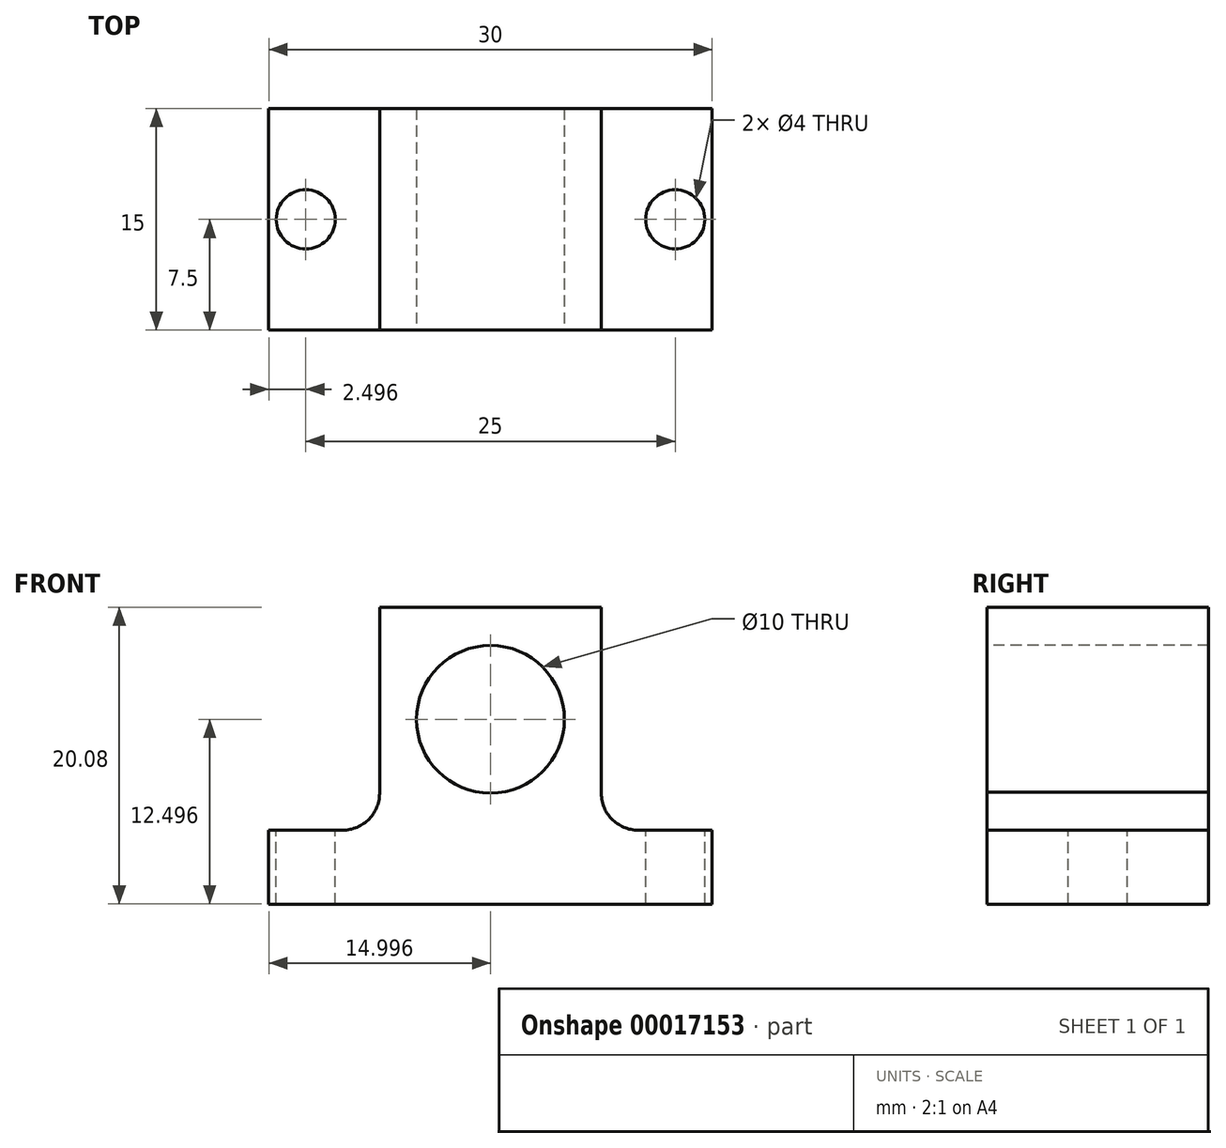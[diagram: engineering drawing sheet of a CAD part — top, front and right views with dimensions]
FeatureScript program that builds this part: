
annotation { "Feature Type Name" : "Feature", "Feature Type Description" : "" }
export const myFeature = defineFeature(function(context is Context, id is Id, definition is map)
    precondition{}
    {
        {
            var Q0;
            Q0=qCreatedBy(makeId("Front.planeOp"),FACE);
            var sketch = newSketch(context, id + "F0", { "sketchPlane" : qUnion([Q0])});
            skLineSegment(sketch, "E0", {"start": v(-20.16, -31.2) * mm, "end": v(9.84, -31.2) * mm});
            skLineSegment(sketch, "E1", {"start": v(9.84, -31.2) * mm, "end": v(9.84, -26.2) * mm});
            skLineSegment(sketch, "E2", {"start": v(9.84, -26.2) * mm, "end": v(4.84, -26.2) * mm});
            skLineSegment(sketch, "E3", {"start": v(-20.16, -31.2) * mm, "end": v(-20.16, -26.2) * mm});
            skLineSegment(sketch, "E4", {"start": v(-20.16, -26.2) * mm, "end": v(-15.16, -26.2) * mm});
            skArc(sketch, "E5", {"start": v(4.84, -26.2) * mm, "mid": v(3.04, -25.44) * mm, "end": v(2.33, -23.62) * mm});
            skArc(sketch, "E6", {"start": v(-15.16, -26.2) * mm, "mid": v(-13.37, -25.44) * mm, "end": v(-12.67, -23.62) * mm});
            skLineSegment(sketch, "E7", {"start": v(-12.67, -23.62) * mm, "end": v(-12.67, -11.12) * mm});
            skLineSegment(sketch, "E8", {"start": v(-12.67, -11.12) * mm, "end": v(2.33, -11.12) * mm});
            skLineSegment(sketch, "E9", {"start": v(2.33, -11.12) * mm, "end": v(2.33, -23.62) * mm});
            skSolve(sketch);
        }
        {
            var Q0;
            Q0=makeQuery(id+"F0.imprint","IMPRINT",FACE,{"disambiguationData":[TD([[makeQuery(id+"F0.imprint","IMPRINT",EDGE,{"derivedFrom":sQuery(id+"F0.wireOp",EDGE,"E0")}),1.0]])]});
            extrude(context, id + "F1", {"entities" : qUnion([Q0]), "depth" : 15 * mm});
        }
        {
            var Q0;
            Q0=makeQuery(id+"F1.opExtrude","SWEPT_FACE",FACE,{"disambiguationData":[OSD([sQuery(id+"F0.wireOp",EDGE,"E4")])]});
            var sketch = newSketch(context, id + "F2", { "sketchPlane" : qUnion([Q0])});
            skCircle(sketch, "E10", {"center": v(-17.66, -7.5) * mm, "radius": 2 * mm});
            skSolve(sketch);
        }
        {
            var Q0;
            Q0=makeQuery(id+"F2.imprint","IMPRINT",FACE,{"disambiguationData":[TD([[makeQuery(id+"F2.imprint","IMPRINT",EDGE,{"derivedFrom":sQuery(id+"F2.wireOp",EDGE,"E10")}),1.0]])]});
            extrude(context, id + "F3", {"entities" : qUnion([Q0]), "operationType" : NewBodyOperationType.REMOVE, "endBound" : BoundingType.THROUGH_ALL, "oppositeDirection" : true, "depth" : 25 * mm});
        }
        {
            var Q0;
            Q0=makeQuery(id+"F1.opExtrude","SWEPT_FACE",FACE,{"disambiguationData":[OSD([sQuery(id+"F0.wireOp",EDGE,"E2")])]});
            var sketch = newSketch(context, id + "F4", { "sketchPlane" : qUnion([Q0])});
            skCircle(sketch, "E11", {"center": v(7.34, -7.5) * mm, "radius": 2 * mm});
            skSolve(sketch);
        }
        {
            var Q0;
            Q0 = qSketchRegion(id + "F4", true);
            extrude(context, id + "F5", {"entities" : qUnion([Q0]), "operationType" : NewBodyOperationType.REMOVE, "endBound" : BoundingType.THROUGH_ALL, "oppositeDirection" : true, "depth" : 25 * mm});
        }
        {
            var Q0;
            Q0=makeQuery(id+"F1.opExtrude","CAP_FACE",FACE,{"disambiguationData":[OSD([sQuery(id+"F0.wireOp",EDGE,"E0"),sQuery(id+"F0.wireOp",EDGE,"E1"),sQuery(id+"F0.wireOp",EDGE,"E2"),sQuery(id+"F0.wireOp",EDGE,"E3"),sQuery(id+"F0.wireOp",EDGE,"E4"),sQuery(id+"F0.wireOp",EDGE,"E5"),sQuery(id+"F0.wireOp",EDGE,"E6"),sQuery(id+"F0.wireOp",EDGE,"E7"),sQuery(id+"F0.wireOp",EDGE,"E8"),sQuery(id+"F0.wireOp",EDGE,"E9")])],"isStart":false});
            var sketch = newSketch(context, id + "F6", { "sketchPlane" : qUnion([Q0])});
            skCircle(sketch, "E12", {"center": v(-5.16, -18.7) * mm, "radius": 5 * mm});
            skSolve(sketch);
        }
        {
            var Q0;
            Q0 = qSketchRegion(id + "F6", true);
            extrude(context, id + "F7", {"entities" : qUnion([Q0]), "operationType" : NewBodyOperationType.REMOVE, "endBound" : BoundingType.THROUGH_ALL, "oppositeDirection" : true, "depth" : 25 * mm});
        }
    });
